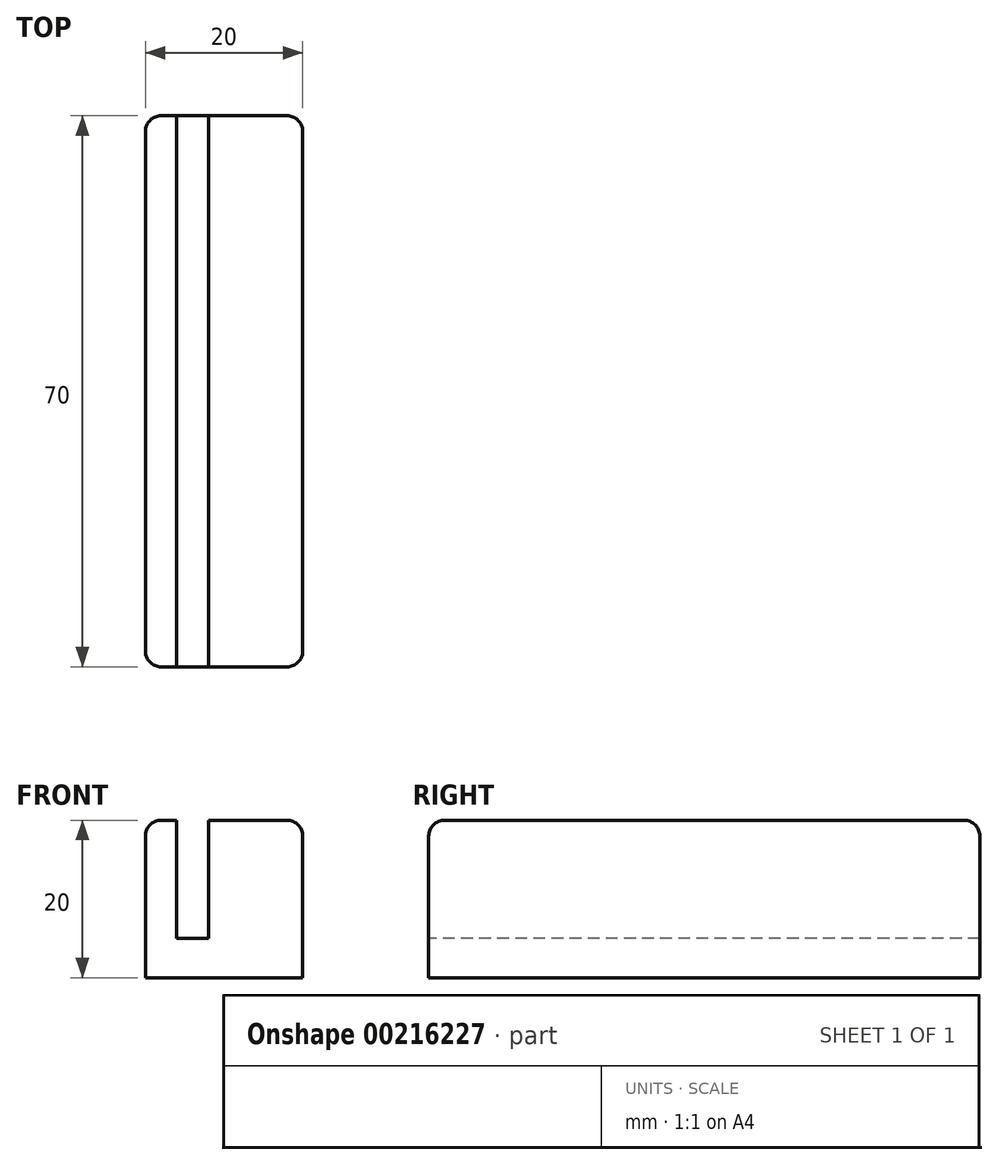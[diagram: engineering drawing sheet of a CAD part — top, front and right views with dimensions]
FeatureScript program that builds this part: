
annotation { "Feature Type Name" : "Feature", "Feature Type Description" : "" }
export const myFeature = defineFeature(function(context is Context, id is Id, definition is map)
    precondition{}
    {
        {
            var Q0;
            Q0=qCreatedBy(makeId("Top.planeOp"),FACE);
            var sketch = newSketch(context, id + "F0", { "sketchPlane" : qUnion([Q0])});
            skLineSegment(sketch, "E0.bottom", {"start": v(-10, 35) * mm, "end": v(10, 35) * mm});
            skLineSegment(sketch, "E0.top", {"start": v(-10, -35) * mm, "end": v(10, -35) * mm});
            skLineSegment(sketch, "E0.left", {"start": v(-10, 35) * mm, "end": v(-10, -35) * mm});
            skLineSegment(sketch, "E0.right", {"start": v(10, 35) * mm, "end": v(10, -35) * mm});
            skLineSegment(sketch, "E1", {"start": v(-10, 35) * mm, "end": v(10, -35) * mm, "construction": true});
            skSolve(sketch);
        }
        {
            var Q0;
            Q0 = qSketchRegion(id + "F0", true);
            extrude(context, id + "F1", {"entities" : qUnion([Q0]), "depth" : 20 * mm, "offsetDistance" : 25.4 * mm});
        }
        {
            var Q0;
            Q0=makeQuery(id+"F1.opExtrude","CAP_FACE",FACE,{"disambiguationData":[OSD([sQuery(id+"F0.wireOp",EDGE,"E0.bottom"),sQuery(id+"F0.wireOp",EDGE,"E0.top"),sQuery(id+"F0.wireOp",EDGE,"E0.left"),sQuery(id+"F0.wireOp",EDGE,"E0.right")])],"isStart":false});
            var sketch = newSketch(context, id + "F2", { "sketchPlane" : qUnion([Q0])});
            skLineSegment(sketch, "E2.bottom", {"start": v(-6, 35) * mm, "end": v(-2, 35) * mm});
            skLineSegment(sketch, "E2.top", {"start": v(-6, -35) * mm, "end": v(-2, -35) * mm});
            skLineSegment(sketch, "E2.left", {"start": v(-6, 35) * mm, "end": v(-6, -35) * mm});
            skLineSegment(sketch, "E2.right", {"start": v(-2, 35) * mm, "end": v(-2, -35) * mm});
            skSolve(sketch);
        }
        {
            var Q0;
            Q0=makeQuery(id+"F2.imprint","IMPRINT",FACE,{"disambiguationData":[TD([[makeQuery(id+"F2.imprint","IMPRINT",EDGE,{"derivedFrom":sQuery(id+"F2.wireOp",EDGE,"E2.bottom")}),-1.0]])]});
            extrude(context, id + "F3", {"entities" : qUnion([Q0]), "operationType" : NewBodyOperationType.REMOVE, "oppositeDirection" : true, "depth" : 15 * mm, "offsetDistance" : 25.4 * mm});
        }
        {
            var Q0;
            Q0=makeQuery(id+"F1.opExtrude","CAP_EDGE",EDGE,{"disambiguationData":[OSD([sQuery(id+"F0.wireOp",EDGE,"E0.right")])],"isStart":false});
            var Q1;
            Q1=makeQuery(id+"F1.opExtrude","CAP_EDGE",EDGE,{"disambiguationData":[OSD([sQuery(id+"F0.wireOp",EDGE,"E0.left")])],"isStart":false});
            var Q2;
            {var subQ0=sQuery(id+"F0.wireOp",EDGE,"E0.right");var subQ1=sQuery(id+"F0.wireOp",EDGE,"E0.top");Q2=makeQuery(id+"F3.boolean.opBoolean","SPLIT",EDGE,{"disambiguationData":[TD([makeQuery(id+"F1.opExtrude","SWEPT_FACE",FACE,{"disambiguationData":[OSD([subQ0])]})])],"derivedFrom":makeQuery(id+"F1.opExtrude","CAP_EDGE",EDGE,{"disambiguationData":[OSD([subQ1])],"isStart":false})});}
            var Q3;
            {var subQ0=sQuery(id+"F0.wireOp",EDGE,"E0.left");var subQ1=sQuery(id+"F0.wireOp",EDGE,"E0.top");Q3=makeQuery(id+"F3.boolean.opBoolean","SPLIT",EDGE,{"disambiguationData":[TD([makeQuery(id+"F1.opExtrude","SWEPT_FACE",FACE,{"disambiguationData":[OSD([subQ0])]})])],"derivedFrom":makeQuery(id+"F1.opExtrude","CAP_EDGE",EDGE,{"disambiguationData":[OSD([subQ1])],"isStart":false})});}
            var Q4;
            {var subQ0=sQuery(id+"F0.wireOp",EDGE,"E0.bottom");var subQ1=sQuery(id+"F0.wireOp",EDGE,"E0.right");Q4=makeQuery(id+"F3.boolean.opBoolean","SPLIT",EDGE,{"disambiguationData":[TD([makeQuery(id+"F1.opExtrude","SWEPT_FACE",FACE,{"disambiguationData":[OSD([subQ1])]})])],"derivedFrom":makeQuery(id+"F1.opExtrude","CAP_EDGE",EDGE,{"disambiguationData":[OSD([subQ0])],"isStart":false})});}
            var Q5;
            {var subQ0=sQuery(id+"F0.wireOp",EDGE,"E0.bottom");var subQ1=sQuery(id+"F0.wireOp",EDGE,"E0.left");Q5=makeQuery(id+"F3.boolean.opBoolean","SPLIT",EDGE,{"disambiguationData":[TD([makeQuery(id+"F1.opExtrude","SWEPT_FACE",FACE,{"disambiguationData":[OSD([subQ1])]})])],"derivedFrom":makeQuery(id+"F1.opExtrude","CAP_EDGE",EDGE,{"disambiguationData":[OSD([subQ0])],"isStart":false})});}
            var Q6;
            Q6=makeQuery(id+"F1.opExtrude","SWEPT_EDGE",EDGE,{"disambiguationData":[OSD([sQuery(id+"F0.wireOp",EDGE,"E0.top"),sQuery(id+"F0.wireOp",EDGE,"E0.right")])]});
            var Q7;
            Q7=makeQuery(id+"F1.opExtrude","SWEPT_EDGE",EDGE,{"disambiguationData":[OSD([sQuery(id+"F0.wireOp",EDGE,"E0.top"),sQuery(id+"F0.wireOp",EDGE,"E0.left")])]});
            var Q8;
            Q8=makeQuery(id+"F1.opExtrude","SWEPT_EDGE",EDGE,{"disambiguationData":[OSD([sQuery(id+"F0.wireOp",EDGE,"E0.bottom"),sQuery(id+"F0.wireOp",EDGE,"E0.right")])]});
            var Q9;
            Q9=makeQuery(id+"F1.opExtrude","SWEPT_EDGE",EDGE,{"disambiguationData":[OSD([sQuery(id+"F0.wireOp",EDGE,"E0.bottom"),sQuery(id+"F0.wireOp",EDGE,"E0.left")])]});
            fillet(context, id + "F4", {"entities" : qUnion([Q0, Q1, Q2, Q3, Q4, Q5, Q6, Q7, Q8, Q9]), "tangentPropagation" : true, "radius" : 2 * mm, "defaultsChanged" : false, "vertexSettings" : [], "allowEdgeOverflow" : false});
        }
    });
